# Revit family: PV_2915-2965-2606_OS275
name_source: partatom
category: Porte
units: mm (PartAtom-declared; Revit-internal decimal feet)

## family parameters
Condiviso = No
Host = Muro
Numero OmniClass = 23.30.10.00
Punto di calcolo locali = Sì
Sempre verticale = Sì
Taglio con vuoti quando caricato = No
Titolo OmniClass = Doors

## types (4) — shared parameters
Altezza = 2000 mm  [stored 6.56168 ft]
Altezza_ante = 1970 mm  [stored 6.46325 ft]
Chiusura muro = Per host
Costruzione analitica = <Nessuno>
Descrizione = Bilico verticale
Funzione = Interno
H1 = 2000 mm  [stored 6.56168 ft]
H_Max = 3500 mm
H_Min = 1600 mm  [stored 5.24934 ft]
H_maniglia = 1000 mm  [stored 3.28084 ft]
H_vetro = 1894 mm  [stored 6.21391 ft]
L_Max = 2100 mm
L_Min = 600 mm  [stored 1.9685 ft]
Larghezza telaio = 75 mm
Modello = OS2 75
Produttore = Secco Sistemi Spa
Proiezione telaio est. = 25 mm  [stored 0.082021 ft]
Proiezione telaio int. = 25 mm  [stored 0.082021 ft]
URL = https://www.seccosistemi.com
WARNING = No

## per-type parameters (varying)
| type | L1 | L_Telaio_E | L_Telaio_I | L_vetro | Larghezza | Larghezza_1A | Larghezza_2A | MATERIALE |
| Ottone | 1200 mm | 600 mm  [stored 1.9685 ft] | 600 mm  [stored 1.9685 ft] | 1094 mm  [stored 3.58924 ft] | 1200 mm | 585 mm  [stored 1.91929 ft] | 585 mm  [stored 1.91929 ft] | Ottone |
| Acciaio inox | 1500 mm | 750 mm  [stored 2.46063 ft] | 750 mm  [stored 2.46063 ft] | 1394 mm | 1500 mm | 735 mm | 735 mm | Acciaio inox, spazzolato |
| Acciaio corten | 1500 mm | 750 mm  [stored 2.46063 ft] | 750 mm  [stored 2.46063 ft] | 1394 mm | 1500 mm | 735 mm | 735 mm | Acciaio corten |
| Acciaio zincato | 1500 mm | 750 mm  [stored 2.46063 ft] | 750 mm  [stored 2.46063 ft] | 1394 mm | 1500 mm | 735 mm | 735 mm | Acciaio |

note: [stored X ft] marks values corroborated as IEEE doubles in the binary element streams (Revit-internal decimal feet)
